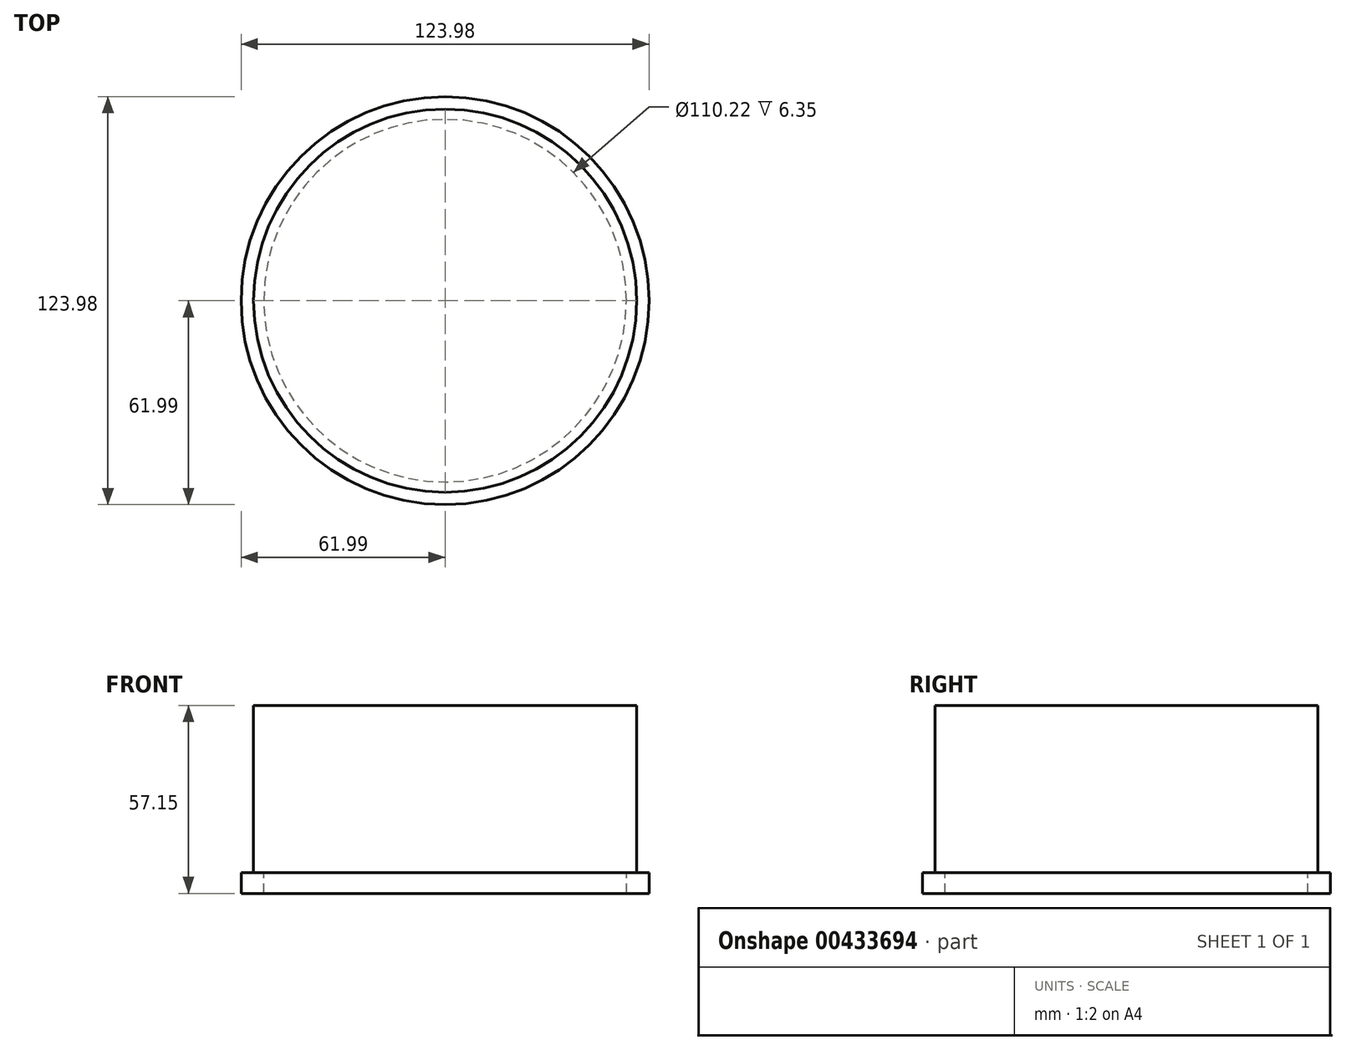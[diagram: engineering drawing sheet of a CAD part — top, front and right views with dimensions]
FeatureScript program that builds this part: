
annotation { "Feature Type Name" : "Feature", "Feature Type Description" : "" }
export const myFeature = defineFeature(function(context is Context, id is Id, definition is map)
    precondition{}
    {
        {
            var Q0;
            Q0=qCreatedBy(makeId("Top.planeOp"),FACE);
            var sketch = newSketch(context, id + "F0", { "sketchPlane" : qUnion([Q0])});
            skCircle(sketch, "E0", {"center": v(0, 0) * mm, "radius": 58.21 * mm});
            skSolve(sketch);
        }
        {
            var Q0;
            Q0=makeQuery(id+"F0.imprint","IMPRINT",FACE,{"disambiguationData":[TD([[makeQuery(id+"F0.imprint","IMPRINT",EDGE,{"derivedFrom":sQuery(id+"F0.wireOp",EDGE,"E0")}),1.0]])]});
            extrude(context, id + "F1", {"entities" : qUnion([Q0]), "depth" : 50.8 * mm});
        }
        {
            var Q0;
            Q0=makeQuery(id+"F1.opExtrude","CAP_FACE",FACE,{"disambiguationData":[OSD([sQuery(id+"F0.wireOp",EDGE,"E0")])],"isStart":true});
            var sketch = newSketch(context, id + "F2", { "sketchPlane" : qUnion([Q0])});
            skCircle(sketch, "E1", {"center": v(0, 0) * mm, "radius": 55.11 * mm});
            skCircle(sketch, "E2", {"center": v(0, 0) * mm, "radius": 61.99 * mm});
            skSolve(sketch);
        }
        {
            var Q0;
            Q0 = qSketchRegion(id + "F2", true);
            extrude(context, id + "F3", {"entities" : qUnion([Q0]), "operationType" : NewBodyOperationType.ADD, "depth" : 6.35 * mm});
        }
    });
